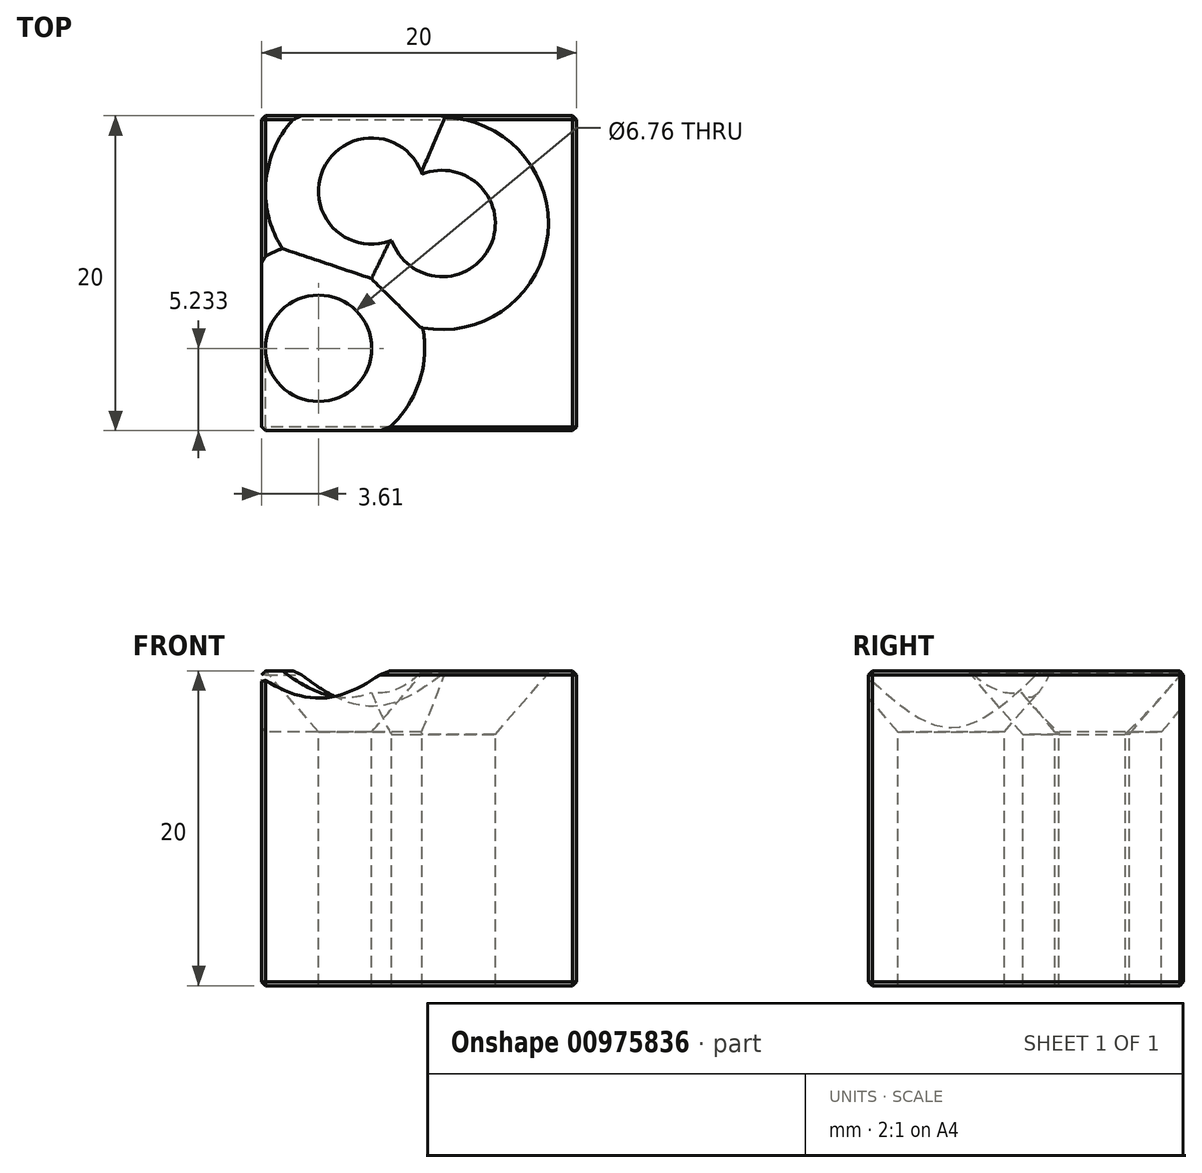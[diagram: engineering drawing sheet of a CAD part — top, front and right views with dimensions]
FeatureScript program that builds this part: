
annotation { "Feature Type Name" : "Feature", "Feature Type Description" : "" }
export const myFeature = defineFeature(function(context is Context, id is Id, definition is map)
    precondition{}
    {
        {
            var Q0;
            Q0=qCreatedBy(makeId("Top.planeOp"),FACE);
            var sketch = newSketch(context, id + "F0", { "sketchPlane" : qUnion([Q0])});
            skLineSegment(sketch, "E0.bottom", {"start": v(10, -10) * mm, "end": v(-10, -10) * mm});
            skLineSegment(sketch, "E0.top", {"start": v(10, 10) * mm, "end": v(-10, 10) * mm});
            skLineSegment(sketch, "E0.left", {"start": v(10, -10) * mm, "end": v(10, 10) * mm});
            skLineSegment(sketch, "E0.right", {"start": v(-10, -10) * mm, "end": v(-10, 10) * mm});
            skPoint(sketch, "E0.middle", {"position": v(0, 0) * mm});
            skSolve(sketch);
        }
        {
            var Q0;
            Q0 = qSketchRegion(id + "F0", true);
            extrude(context, id + "F1", {"entities" : qUnion([Q0]), "endBound" : BoundingType.SYMMETRIC, "depth" : 20 * mm, "offsetDistance" : 25.4 * mm});
        }
        {
            var Q0;
            Q0=makeQuery(id+"F1.opExtrude","CAP_FACE",FACE,{"disambiguationData":[OSD([sQuery(id+"F0.wireOp",EDGE,"E0.bottom"),sQuery(id+"F0.wireOp",EDGE,"E0.top"),sQuery(id+"F0.wireOp",EDGE,"E0.left"),sQuery(id+"F0.wireOp",EDGE,"E0.right")])],"isStart":false});
            var Q1;
            Q1=makeQuery(id+"F1.opExtrude","SWEPT_FACE",FACE,{"disambiguationData":[OSD([sQuery(id+"F0.wireOp",EDGE,"E0.right")])]});
            var Q2;
            Q2=makeQuery(id+"F1.opExtrude","SWEPT_FACE",FACE,{"disambiguationData":[OSD([sQuery(id+"F0.wireOp",EDGE,"E0.top")])]});
            var Q3;
            Q3=makeQuery(id+"F1.opExtrude","SWEPT_FACE",FACE,{"disambiguationData":[OSD([sQuery(id+"F0.wireOp",EDGE,"E0.left")])]});
            var Q4;
            Q4=makeQuery(id+"F1.opExtrude","SWEPT_FACE",FACE,{"disambiguationData":[OSD([sQuery(id+"F0.wireOp",EDGE,"E0.bottom")])]});
            var Q5;
            Q5=makeQuery(id+"F1.opExtrude","CAP_FACE",FACE,{"disambiguationData":[OSD([sQuery(id+"F0.wireOp",EDGE,"E0.bottom"),sQuery(id+"F0.wireOp",EDGE,"E0.top"),sQuery(id+"F0.wireOp",EDGE,"E0.left"),sQuery(id+"F0.wireOp",EDGE,"E0.right")])],"isStart":true});
            chamfer(context, id + "F2", {"entities" : qUnion([Q0, Q1, Q2, Q3, Q4, Q5]), "width" : .25 * mm, "tangentPropagation" : true});
        }
        {
            var Q0;
            Q0=makeQuery(id+"F1.opExtrude","CAP_FACE",FACE,{"disambiguationData":[OSD([sQuery(id+"F0.wireOp",EDGE,"E0.bottom"),sQuery(id+"F0.wireOp",EDGE,"E0.top"),sQuery(id+"F0.wireOp",EDGE,"E0.left"),sQuery(id+"F0.wireOp",EDGE,"E0.right")])],"isStart":false});
            var sketch = newSketch(context, id + "F3", { "sketchPlane" : qUnion([Q0])});
            skPoint(sketch, "E1", {"position": v(-3.02, 5.22) * mm});
            skPoint(sketch, "E2", {"position": v(1.46, 3.16) * mm});
            skPoint(sketch, "E3", {"position": v(-6.4, -4.77) * mm});
            skSolve(sketch);
        }
        {
            var Q0;
            Q0=sQuery(id+"F3.wireOp",VERTEX,"E1");
            var Q1;
            Q1=sQuery(id+"F3.wireOp",VERTEX,"E3");
            var Q2;
            Q2=sQuery(id+"F3.wireOp",VERTEX,"E2");
            var Q3;
            Q3=makeQuery(id+"F1.opExtrude","SWEPT_BODY",BODY,{"disambiguationData":[OSD([sQuery(id+"F0.wireOp",EDGE,"E0.bottom"),sQuery(id+"F0.wireOp",EDGE,"E0.top"),sQuery(id+"F0.wireOp",EDGE,"E0.left"),sQuery(id+"F0.wireOp",EDGE,"E0.right")])]});
            hole(context, id + "F4", {"style" : HoleStyle.C_SINK, "endStyle" : HoleEndStyle.THROUGH, "standardTappedOrClearance" : lookupTablePath({ "fit" : "Close (ASME)", "standard" : "ANSI", "size" : "1/4", "type" : "Clearance" }), "standardBlindInLast" : lookupTablePath({ "fit" : "Close", "standard" : "ANSI", "engagement" : "75%", "pitch" : "20 tpi", "size" : "1/4", "type" : "Clearance & tapped" }), "holeDiameter" : 6.76 * mm, "cSinkDiameter" : 13.5 * mm, "cSinkAngle" : 82 * degree, "majorDiameter" : 6.35 * mm, "isTappedThrough" : true, "tappedDepth" : 12.7 * mm, "tapClearance" : 3, "locations" : qUnion([Q0, Q1, Q2]), "scope" : qUnion([Q3])});
        }
    });
